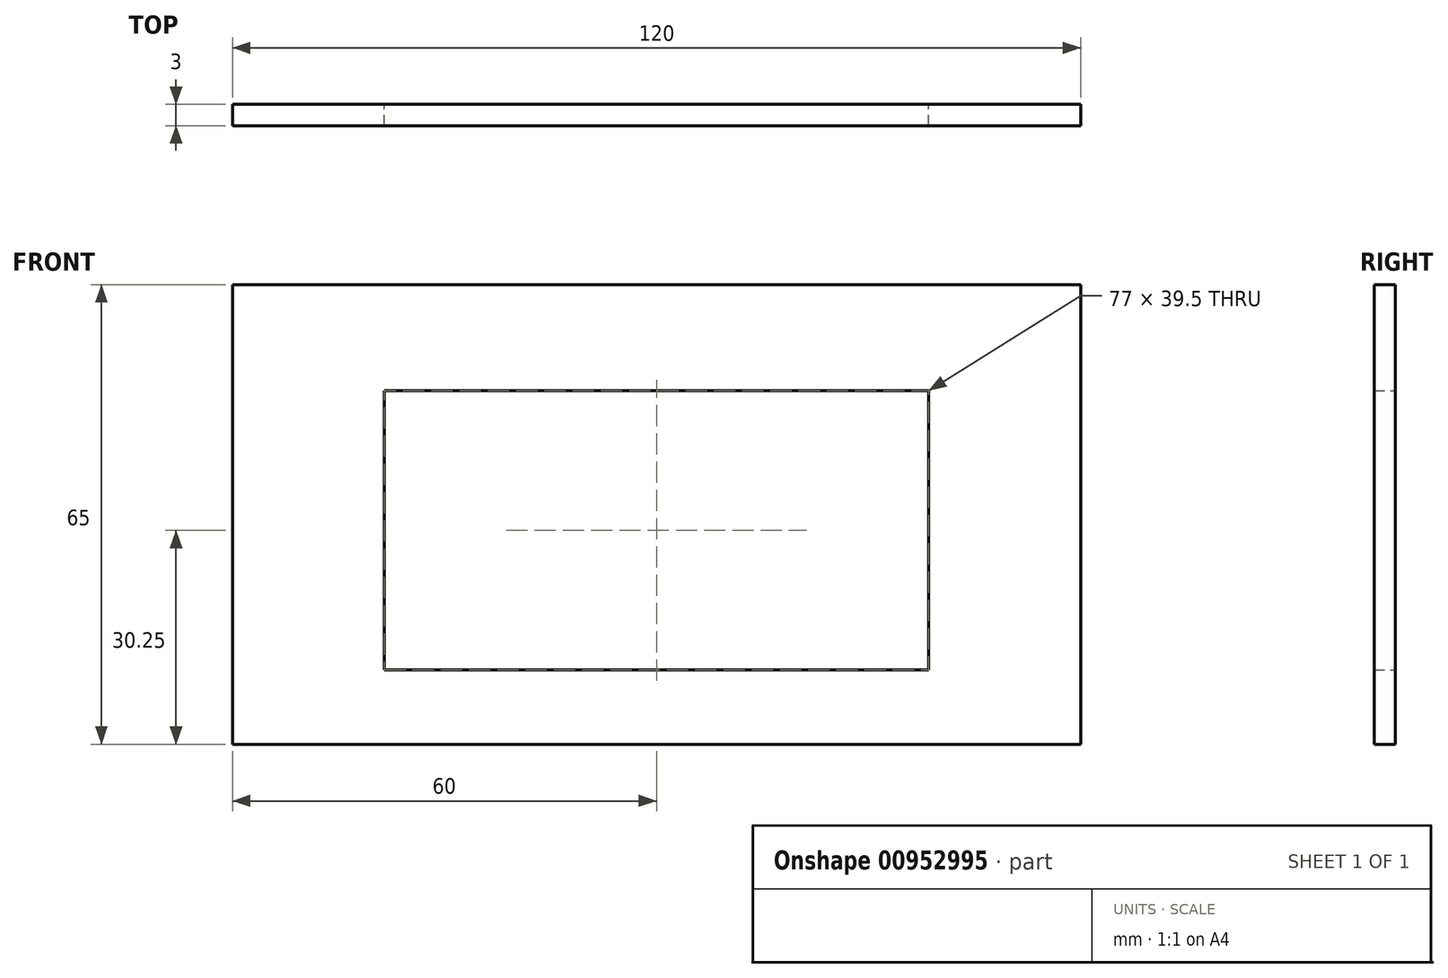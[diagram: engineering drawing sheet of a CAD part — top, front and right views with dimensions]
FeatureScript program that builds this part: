
annotation { "Feature Type Name" : "Feature", "Feature Type Description" : "" }
export const myFeature = defineFeature(function(context is Context, id is Id, definition is map)
    precondition{}
    {
        {
            var Q0;
            Q0=qCreatedBy(makeId("Front.planeOp"),FACE);
            var sketch = newSketch(context, id + "F0", { "sketchPlane" : qUnion([Q0])});
            skLineSegment(sketch, "E0.bottom", {"start": v(60, -32.5) * mm, "end": v(-60, -32.5) * mm});
            skLineSegment(sketch, "E0.top", {"start": v(60, 32.5) * mm, "end": v(-60, 32.5) * mm});
            skLineSegment(sketch, "E0.left", {"start": v(60, -32.5) * mm, "end": v(60, 32.5) * mm});
            skLineSegment(sketch, "E0.right", {"start": v(-60, -32.5) * mm, "end": v(-60, 32.5) * mm});
            skPoint(sketch, "E0.middle", {"position": v(0, 0) * mm});
            skLineSegment(sketch, "E1.bottom", {"start": v(38.5, -22) * mm, "end": v(-38.5, -22) * mm});
            skLineSegment(sketch, "E1.top", {"start": v(38.5, 17.5) * mm, "end": v(-38.5, 17.5) * mm});
            skLineSegment(sketch, "E1.left", {"start": v(38.5, -22) * mm, "end": v(38.5, 17.5) * mm});
            skLineSegment(sketch, "E1.right", {"start": v(-38.5, -22) * mm, "end": v(-38.5, 17.5) * mm});
            skPoint(sketch, "E1.middle", {"position": v(0, -2.25) * mm});
            skSolve(sketch);
        }
        {
            var Q0;
            Q0=makeQuery(id+"F0.imprint","IMPRINT",FACE,{"disambiguationData":[TD([[makeQuery(id+"F0.imprint","IMPRINT",EDGE,{"derivedFrom":sQuery(id+"F0.wireOp",EDGE,"E0.bottom")}),-1.0]])]});
            extrude(context, id + "F1", {"entities" : qUnion([Q0]), "depth" : 3 * mm, "offsetDistance" : 25 * mm});
        }
    });
